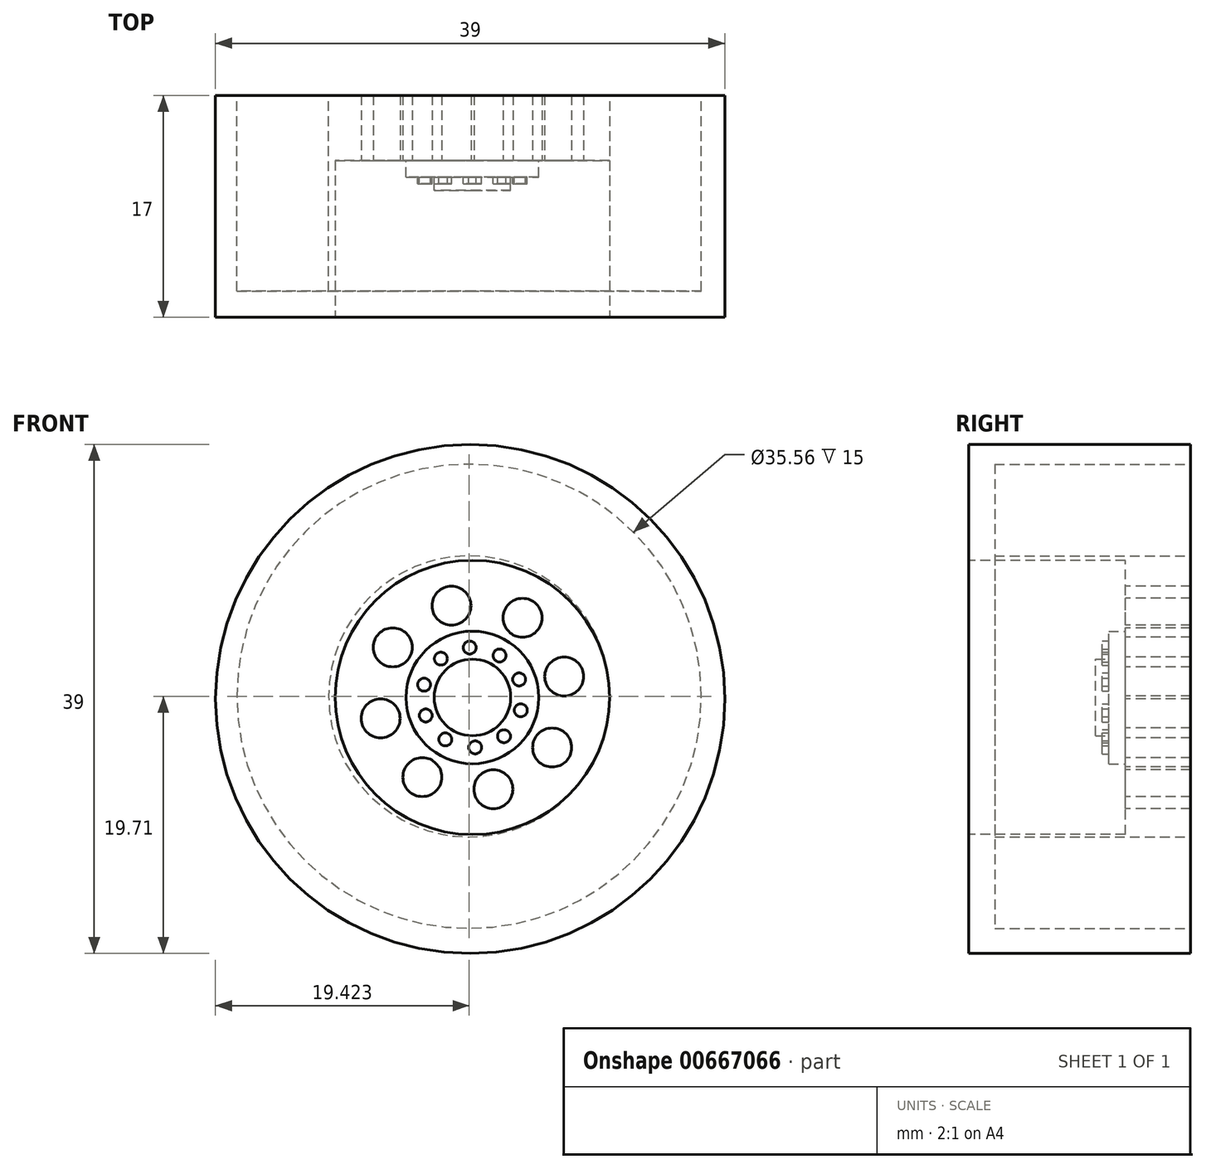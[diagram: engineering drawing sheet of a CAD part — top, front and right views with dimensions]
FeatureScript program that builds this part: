
annotation { "Feature Type Name" : "Feature", "Feature Type Description" : "" }
export const myFeature = defineFeature(function(context is Context, id is Id, definition is map)
    precondition{}
    {
        {
            var Q0;
            Q0=qCreatedBy(makeId("Front.planeOp"),FACE);
            var sketch = newSketch(context, id + "F0", { "sketchPlane" : qUnion([Q0])});
            skCircle(sketch, "E0", {"center": v(8.13, 26.8) * mm, "radius": 19.5 * mm});
            skSolve(sketch);
        }
        {
            var Q0;
            Q0=makeQuery(id+"F0.imprint","IMPRINT",FACE,{"disambiguationData":[TD([[makeQuery(id+"F0.imprint","IMPRINT",EDGE,{"derivedFrom":sQuery(id+"F0.wireOp",EDGE,"E0")}),1.0]])]});
            var sketch = newSketch(context, id + "F1", { "sketchPlane" : qUnion([Q0])});
            skCircle(sketch, "E1", {"center": v(8.3, 26.92) * mm, "radius": 10.5 * mm});
            skSolve(sketch);
        }
        {
            var Q0;
            Q0=makeQuery(id+"F0.imprint","IMPRINT",FACE,{"disambiguationData":[TD([[makeQuery(id+"F0.imprint","IMPRINT",EDGE,{"derivedFrom":sQuery(id+"F0.wireOp",EDGE,"E0")}),1.0]])]});
            extrude(context, id + "F2", {"entities" : qUnion([Q0]), "oppositeDirection" : true, "depth" : 17 * mm, "offsetDistance" : 25.4 * mm});
        }
        {
            var Q0;
            Q0=makeQuery(id+"F1.imprint","IMPRINT",FACE,{"disambiguationData":[TD([[makeQuery(id+"F1.imprint","IMPRINT",EDGE,{"derivedFrom":sQuery(id+"F1.wireOp",EDGE,"E1")}),1.0]])]});
            extrude(context, id + "F3", {"entities" : qUnion([Q0]), "operationType" : NewBodyOperationType.REMOVE, "oppositeDirection" : true, "depth" : 12 * mm, "offsetDistance" : 25.4 * mm});
        }
        {
            var Q0;
            Q0=makeQuery(id+"F3.boolean.opBoolean","COPY",FACE,{"derivedFrom":makeQuery(id+"F3.opExtrude","CAP_FACE",FACE,{"disambiguationData":[OSD([sQuery(id+"F1.wireOp",EDGE,"E1")])],"isStart":false})});
            var sketch = newSketch(context, id + "F4", { "sketchPlane" : qUnion([Q0])});
            skCircle(sketch, "E2", {"center": v(6.7, 33.95) * mm, "radius": 1.5 * mm});
            skCircle(sketch, "E3.1.0", {"center": v(2.2, 30.75) * mm, "radius": 1.5 * mm});
            skCircle(sketch, "E3.2.0", {"center": v(1.27, 25.31) * mm, "radius": 1.5 * mm});
            skCircle(sketch, "E3.3.0", {"center": v(4.47, 20.81) * mm, "radius": 1.5 * mm});
            skCircle(sketch, "E3.4.0", {"center": v(9.9, 19.89) * mm, "radius": 1.5 * mm});
            skCircle(sketch, "E3.5.0", {"center": v(14.4, 23.08) * mm, "radius": 1.5 * mm});
            skCircle(sketch, "E3.6.0", {"center": v(15.33, 28.52) * mm, "radius": 1.5 * mm});
            skCircle(sketch, "E3.7.0", {"center": v(12.14, 33.02) * mm, "radius": 1.5 * mm});
            skPoint(sketch, "E3.center", {"position": v(8.3, 26.92) * mm});
            skSolve(sketch);
        }
        {
            var Q0;
            Q0=makeQuery(id+"F4.imprint","IMPRINT",FACE,{"disambiguationData":[TD([[makeQuery(id+"F4.imprint","IMPRINT",EDGE,{"derivedFrom":sQuery(id+"F4.wireOp",EDGE,"E2")}),1.0]])]});
            var Q1;
            Q1=makeQuery(id+"F4.imprint","IMPRINT",FACE,{"disambiguationData":[TD([[makeQuery(id+"F4.imprint","IMPRINT",EDGE,{"derivedFrom":sQuery(id+"F4.wireOp",EDGE,"E3.7.0")}),1.0]])]});
            var Q2;
            Q2=makeQuery(id+"F4.imprint","IMPRINT",FACE,{"disambiguationData":[TD([[makeQuery(id+"F4.imprint","IMPRINT",EDGE,{"derivedFrom":sQuery(id+"F4.wireOp",EDGE,"E3.6.0")}),1.0]])]});
            var Q3;
            Q3=makeQuery(id+"F4.imprint","IMPRINT",FACE,{"disambiguationData":[TD([[makeQuery(id+"F4.imprint","IMPRINT",EDGE,{"derivedFrom":sQuery(id+"F4.wireOp",EDGE,"E3.5.0")}),1.0]])]});
            var Q4;
            Q4=makeQuery(id+"F4.imprint","IMPRINT",FACE,{"disambiguationData":[TD([[makeQuery(id+"F4.imprint","IMPRINT",EDGE,{"derivedFrom":sQuery(id+"F4.wireOp",EDGE,"E3.4.0")}),1.0]])]});
            var Q5;
            Q5=makeQuery(id+"F4.imprint","IMPRINT",FACE,{"disambiguationData":[TD([[makeQuery(id+"F4.imprint","IMPRINT",EDGE,{"derivedFrom":sQuery(id+"F4.wireOp",EDGE,"E3.3.0")}),1.0]])]});
            var Q6;
            Q6=makeQuery(id+"F4.imprint","IMPRINT",FACE,{"disambiguationData":[TD([[makeQuery(id+"F4.imprint","IMPRINT",EDGE,{"derivedFrom":sQuery(id+"F4.wireOp",EDGE,"E3.2.0")}),1.0]])]});
            var Q7;
            Q7=makeQuery(id+"F4.imprint","IMPRINT",FACE,{"disambiguationData":[TD([[makeQuery(id+"F4.imprint","IMPRINT",EDGE,{"derivedFrom":sQuery(id+"F4.wireOp",EDGE,"E3.1.0")}),1.0]])]});
            extrude(context, id + "F5", {"entities" : qUnion([Q0, Q1, Q2, Q3, Q4, Q5, Q6, Q7]), "operationType" : NewBodyOperationType.REMOVE, "oppositeDirection" : true, "depth" : 25.4 * mm, "offsetDistance" : 25.4 * mm});
        }
        {
            var Q0;
            Q0=makeQuery(id+"F2.opExtrude","CAP_FACE",FACE,{"disambiguationData":[OSD([sQuery(id+"F0.wireOp",EDGE,"E0")])],"isStart":false});
            var sketch = newSketch(context, id + "F6", { "sketchPlane" : qUnion([Q0])});
            skCircle(sketch, "E4", {"center": v(-8.05, 27.01) * mm, "radius": 10.25 * mm});
            skCircle(sketch, "E5", {"center": v(-8.05, 27.01) * mm, "radius": 17.78 * mm});
            skSolve(sketch);
        }
        {
            var Q0;
            Q0=makeQuery(id+"F6.imprint","IMPRINT",FACE,{"disambiguationData":[TD([[makeQuery(id+"F6.imprint","IMPRINT",EDGE,{"derivedFrom":sQuery(id+"F6.wireOp",EDGE,"E4")}),-1.0]])]});
            var sketch = newSketch(context, id + "F7", { "sketchPlane" : qUnion([Q0])});
            skCircle(sketch, "E6", {"center": v(-8.07, 27) * mm, "radius": 10.77 * mm});
            skSolve(sketch);
        }
        {
            var Q0;
            Q0=makeQuery(id+"F7.imprint","IMPRINT",FACE,{"disambiguationData":[TD([[makeQuery(id+"F7.imprint","IMPRINT",EDGE,{"derivedFrom":sQuery(id+"F7.wireOp",EDGE,"E6")}),-1.0]])]});
            extrude(context, id + "F8", {"entities" : qUnion([Q0]), "operationType" : NewBodyOperationType.REMOVE, "oppositeDirection" : true, "depth" : 15 * mm, "offsetDistance" : 25.4 * mm});
        }
        {
            var Q0;
            Q0=makeQuery(id+"F3.boolean.opBoolean","COPY",FACE,{"derivedFrom":makeQuery(id+"F3.opExtrude","CAP_FACE",FACE,{"disambiguationData":[OSD([sQuery(id+"F1.wireOp",EDGE,"E1")])],"isStart":false})});
            var sketch = newSketch(context, id + "F9", { "sketchPlane" : qUnion([Q0])});
            skCircle(sketch, "E7", {"center": v(8.3, 26.92) * mm, "radius": 5.08 * mm});
            skSolve(sketch);
        }
        {
            var Q0;
            Q0=makeQuery(id+"F9.imprint","IMPRINT",FACE,{"disambiguationData":[TD([[makeQuery(id+"F9.imprint","IMPRINT",EDGE,{"derivedFrom":sQuery(id+"F9.wireOp",EDGE,"E7")}),1.0]])]});
            extrude(context, id + "F10", {"entities" : qUnion([Q0]), "operationType" : NewBodyOperationType.ADD, "depth" : 1.27 * mm, "offsetDistance" : 25.4 * mm});
        }
        {
            var Q0;
            Q0=makeQuery(id+"F6.imprint","IMPRINT",FACE,{"disambiguationData":[TD([[makeQuery(id+"F6.imprint","IMPRINT",EDGE,{"derivedFrom":sQuery(id+"F6.wireOp",EDGE,"E4")}),1.0]])]});
            var sketch = newSketch(context, id + "F11", { "sketchPlane" : qUnion([Q0])});
            skCircle(sketch, "E8", {"center": v(-8.24, 26.96) * mm, "radius": 5.08 * mm});
            skSolve(sketch);
        }
        {
            var Q0;
            Q0=sQuery(id+"F11.wireOp",EDGE,"E8");
            extrude(context, id + "F12", {"bodyType" : ToolBodyType.SURFACE, "operationType" : NewBodyOperationType.ADD, "surfaceEntities" : qUnion([Q0]), "depth" : 10.16 * mm, "offsetDistance" : 25.4 * mm});
        }
        {
            var Q0;
            Q0=makeQuery(id+"F10.opExtrude","CAP_FACE",FACE,{"disambiguationData":[OSD([sQuery(id+"F9.wireOp",EDGE,"E7")])],"isStart":false});
            var sketch = newSketch(context, id + "F13", { "sketchPlane" : qUnion([Q0])});
            skCircle(sketch, "E9", {"center": v(8.3, 26.92) * mm, "radius": 2.93 * mm});
            skSolve(sketch);
        }
        {
            var Q0;
            Q0=makeQuery(id+"F13.imprint","IMPRINT",FACE,{"disambiguationData":[TD([[makeQuery(id+"F13.imprint","IMPRINT",EDGE,{"derivedFrom":sQuery(id+"F13.wireOp",EDGE,"E9")}),1.0]])]});
            extrude(context, id + "F14", {"entities" : qUnion([Q0]), "operationType" : NewBodyOperationType.ADD, "depth" : 1.02 * mm, "offsetDistance" : 25.4 * mm});
        }
        {
            var Q0;
            Q0=makeQuery(id+"F10.opExtrude","CAP_FACE",FACE,{"disambiguationData":[OSD([sQuery(id+"F9.wireOp",EDGE,"E7")])],"isStart":false});
            var sketch = newSketch(context, id + "F15", { "sketchPlane" : qUnion([Q0])});
            skCircle(sketch, "E10", {"center": v(8.1, 30.74) * mm, "radius": 0.5 * mm});
            skCircle(sketch, "E11.1.0", {"center": v(5.88, 29.89) * mm, "radius": 0.5 * mm});
            skCircle(sketch, "E11.2.0", {"center": v(4.6, 27.9) * mm, "radius": 0.5 * mm});
            skCircle(sketch, "E11.3.0", {"center": v(4.73, 25.54) * mm, "radius": 0.5 * mm});
            skCircle(sketch, "E11.4.0", {"center": v(6.22, 23.7) * mm, "radius": 0.5 * mm});
            skCircle(sketch, "E11.5.0", {"center": v(8.51, 23.1) * mm, "radius": 0.5 * mm});
            skCircle(sketch, "E11.6.0", {"center": v(10.72, 23.95) * mm, "radius": 0.5 * mm});
            skCircle(sketch, "E11.7.0", {"center": v(12, 25.93) * mm, "radius": 0.5 * mm});
            skCircle(sketch, "E11.8.0", {"center": v(11.87, 28.3) * mm, "radius": 0.5 * mm});
            skCircle(sketch, "E11.9.0", {"center": v(10.38, 30.13) * mm, "radius": 0.5 * mm});
            skPoint(sketch, "E11.center", {"position": v(8.3, 26.92) * mm});
            skSolve(sketch);
        }
        {
            var Q0;
            Q0=makeQuery(id+"F15.imprint","IMPRINT",FACE,{"disambiguationData":[TD([[makeQuery(id+"F15.imprint","IMPRINT",EDGE,{"derivedFrom":sQuery(id+"F15.wireOp",EDGE,"E10")}),1.0]])]});
            var Q1;
            Q1=makeQuery(id+"F15.imprint","IMPRINT",FACE,{"disambiguationData":[TD([[makeQuery(id+"F15.imprint","IMPRINT",EDGE,{"derivedFrom":sQuery(id+"F15.wireOp",EDGE,"E11.9.0")}),1.0]])]});
            var Q2;
            Q2=makeQuery(id+"F15.imprint","IMPRINT",FACE,{"disambiguationData":[TD([[makeQuery(id+"F15.imprint","IMPRINT",EDGE,{"derivedFrom":sQuery(id+"F15.wireOp",EDGE,"E11.8.0")}),1.0]])]});
            var Q3;
            Q3=makeQuery(id+"F15.imprint","IMPRINT",FACE,{"disambiguationData":[TD([[makeQuery(id+"F15.imprint","IMPRINT",EDGE,{"derivedFrom":sQuery(id+"F15.wireOp",EDGE,"E11.7.0")}),1.0]])]});
            var Q4;
            Q4=makeQuery(id+"F15.imprint","IMPRINT",FACE,{"disambiguationData":[TD([[makeQuery(id+"F15.imprint","IMPRINT",EDGE,{"derivedFrom":sQuery(id+"F15.wireOp",EDGE,"E11.6.0")}),1.0]])]});
            var Q5;
            Q5=makeQuery(id+"F15.imprint","IMPRINT",FACE,{"disambiguationData":[TD([[makeQuery(id+"F15.imprint","IMPRINT",EDGE,{"derivedFrom":sQuery(id+"F15.wireOp",EDGE,"E11.5.0")}),1.0]])]});
            var Q6;
            Q6=makeQuery(id+"F15.imprint","IMPRINT",FACE,{"disambiguationData":[TD([[makeQuery(id+"F15.imprint","IMPRINT",EDGE,{"derivedFrom":sQuery(id+"F15.wireOp",EDGE,"E11.4.0")}),1.0]])]});
            var Q7;
            Q7=makeQuery(id+"F15.imprint","IMPRINT",FACE,{"disambiguationData":[TD([[makeQuery(id+"F15.imprint","IMPRINT",EDGE,{"derivedFrom":sQuery(id+"F15.wireOp",EDGE,"E11.3.0")}),1.0]])]});
            var Q8;
            Q8=makeQuery(id+"F15.imprint","IMPRINT",FACE,{"disambiguationData":[TD([[makeQuery(id+"F15.imprint","IMPRINT",EDGE,{"derivedFrom":sQuery(id+"F15.wireOp",EDGE,"E11.2.0")}),1.0]])]});
            var Q9;
            Q9=makeQuery(id+"F15.imprint","IMPRINT",FACE,{"disambiguationData":[TD([[makeQuery(id+"F15.imprint","IMPRINT",EDGE,{"derivedFrom":sQuery(id+"F15.wireOp",EDGE,"E11.1.0")}),1.0]])]});
            extrude(context, id + "F16", {"entities" : qUnion([Q0, Q1, Q2, Q3, Q4, Q5, Q6, Q7, Q8, Q9]), "operationType" : NewBodyOperationType.ADD, "depth" : 0.5 * mm, "offsetDistance" : 25.4 * mm});
        }
    });
